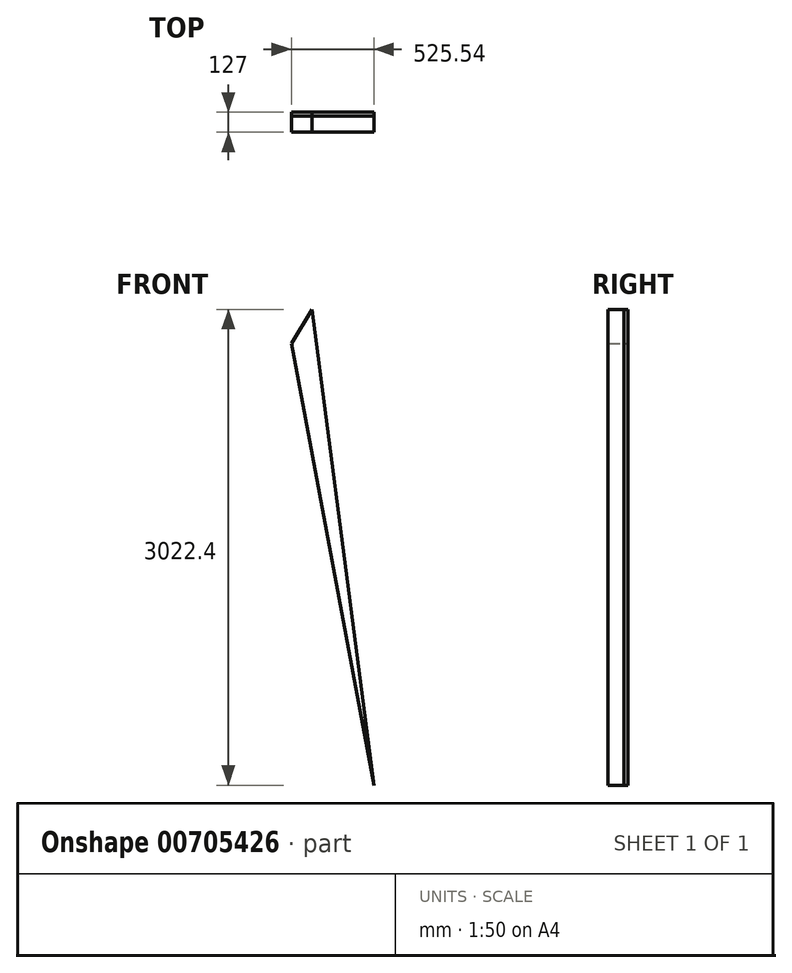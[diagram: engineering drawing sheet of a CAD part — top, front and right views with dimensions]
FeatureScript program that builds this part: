
annotation { "Feature Type Name" : "Feature", "Feature Type Description" : "" }
export const myFeature = defineFeature(function(context is Context, id is Id, definition is map)
    precondition{}
    {
        {
            var Q0;
            Q0=qCreatedBy(makeId("Front.planeOp"),FACE);
            var sketch = newSketch(context, id + "F0", { "sketchPlane" : qUnion([Q0])});
            skLineSegment(sketch, "E0", {"start": v(632.46, 1307.97) * mm, "end": v(632.46, 1307.97) * mm});
            skLineSegment(sketch, "E1", {"start": v(632.46, 1307.97) * mm, "end": v(501.16, 1090.54) * mm});
            skLineSegment(sketch, "E2", {"start": v(501.16, 1090.54) * mm, "end": v(1026.7, -1714.43) * mm});
            skLineSegment(sketch, "E3", {"start": v(1026.7, -1714.43) * mm, "end": v(632.46, 1307.97) * mm});
            skSolve(sketch);
        }
        {
            var Q0;
            Q0 = qSketchRegion(id + "F0", true);
            extrude(context, id + "F1", {"entities" : qUnion([Q0]), "depth" : 127 * mm, "offsetDistance" : 25.4 * mm});
        }
        {
            var Q0;
            Q0 = qSketchRegion(id + "F0", true);
            extrude(context, id + "F2", {"entities" : qUnion([Q0]), "depth" : 25.4 * mm, "offsetDistance" : 25.4 * mm});
        }
    });
